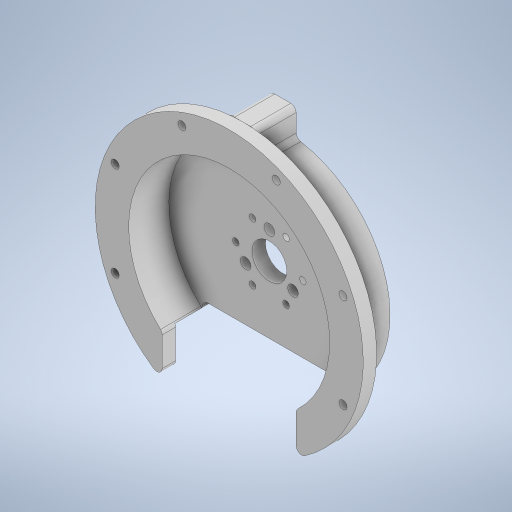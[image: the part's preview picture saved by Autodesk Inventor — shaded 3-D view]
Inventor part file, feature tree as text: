
AUTODESK INVENTOR PART (.ipt)
format: ipt  version: 2024.3 (Build 283343000, 343)  size: 360,448 bytes
history: native  units: mm
features: sketch x9, extrude x6, hole x3, fillet x2
ambient origin geometry x8: Origin, YZ Plane, XZ Plane, XY Plane, X Axis, Y Axis, Z Axis, Center Point
bodies: Body1 (feature_tree)
feature tree (20):
  extrude  "押し出し6"  Depth=80.0mm
  hole  "穴4"  [1 undecoded]
  hole  "穴5"  [1 undecoded]
  extrude  "押し出し7"  TaperAngle=30.0deg  [1 undecoded]
  extrude  "押し出し8"  Depth=60.0mm TaperAngle=360.0deg
  extrude  "押し出し9"  Depth=20.4mm
  hole  "穴6"  [1 undecoded]
  extrude  "押し出し10"  Depth=13.0mm
  fillet  "フィレット2"  [1 undecoded]
  extrude  "押し出し11"  Depth=100.0mm
  fillet  "フィレット3"  Radius=5.0mm
  sketch  "スケッチ9"
  sketch  "スケッチ10"
  sketch  "スケッチ11"
  sketch  "スケッチ12"
  sketch  "スケッチ13"
  sketch  "スケッチ14"
  sketch  "スケッチ15"
  sketch  "スケッチ16"
  sketch  "スケッチ17"
note: 5 required parameter values undecoded (feature->parameter linkage not recoverable at this tier; creation-order binding heuristic only, values carry confidence <= 0.55)
